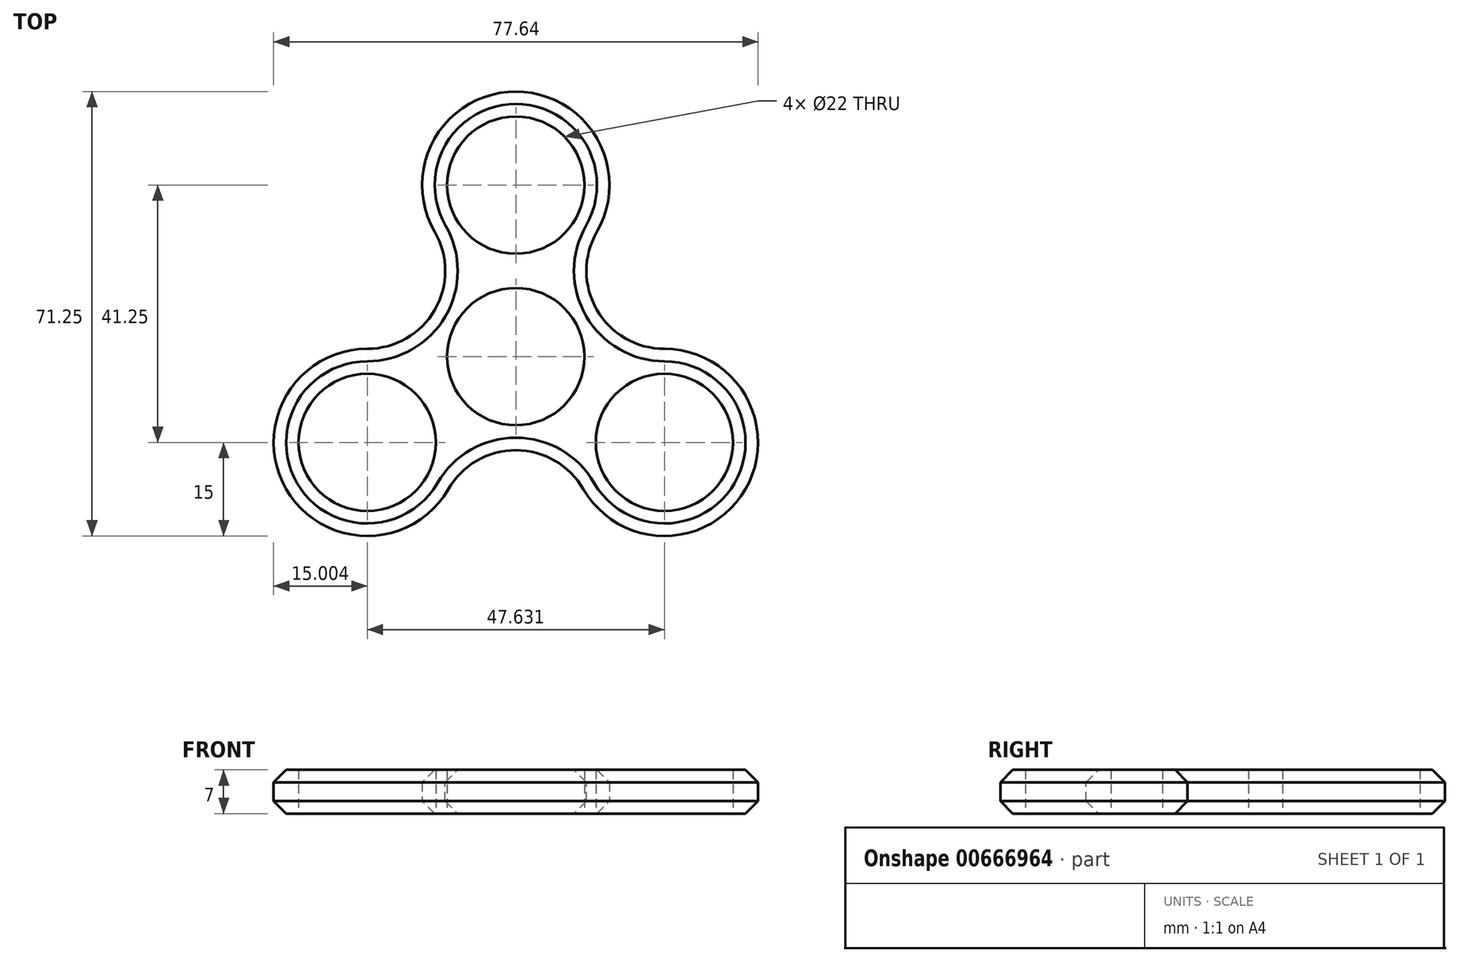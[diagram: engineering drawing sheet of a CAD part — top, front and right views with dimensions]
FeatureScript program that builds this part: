
annotation { "Feature Type Name" : "Feature", "Feature Type Description" : "" }
export const myFeature = defineFeature(function(context is Context, id is Id, definition is map)
    precondition{}
    {
        {
            var Q0;
            Q0=qCreatedBy(makeId("Top.planeOp"),FACE);
            var sketch = newSketch(context, id + "F0", { "sketchPlane" : qUnion([Q0])});
            skCircle(sketch, "E0", {"center": v(0, 0) * mm, "radius": 11 * mm});
            skLineSegment(sketch, "E1", {"start": v(0, 0) * mm, "end": v(0, 27.5) * mm, "construction": true});
            skCircle(sketch, "E2", {"center": v(0, 27.5) * mm, "radius": 11 * mm});
            skCircle(sketch, "E3.1.0", {"center": v(-23.82, -13.75) * mm, "radius": 11 * mm});
            skCircle(sketch, "E3.2.0", {"center": v(23.82, -13.75) * mm, "radius": 11 * mm});
            skCircle(sketch, "E4", {"center": v(0, 0) * mm, "radius": 15 * mm});
            skCircle(sketch, "E5", {"center": v(0, 27.5) * mm, "radius": 15 * mm});
            skCircle(sketch, "E6.1.0", {"center": v(-23.82, -13.75) * mm, "radius": 15 * mm});
            skCircle(sketch, "E6.2.0", {"center": v(23.82, -13.75) * mm, "radius": 15 * mm});
            skSolve(sketch);
        }
        {
            var Q0;
            Q0=qSketchRegion(id+"F0",true);
            extrude(context, id + "F1", {"entities" : qUnion([Q0]), "depth" : 7 * mm, "offsetDistance" : 25 * mm});
        }
        {
            var Q0;
            {var subQ0=sQuery(id+"F0.wireOp",EDGE,"E5");var subQ1=sQuery(id+"F0.wireOp",EDGE,"E4");Q0=makeQuery(id+"F1.opExtrude","SWEPT_EDGE",EDGE,{"disambiguationData":[OSD([subQ1,subQ0]),TDD([makeQuery(id+"F0.imprint","INTERSECT",VERTEX,{"disambiguationData":[OD(1.0)],"derivedFrom":[subQ1,subQ0]})])]});}
            var Q1;
            {var subQ0=sQuery(id+"F0.wireOp",EDGE,"E6.2.0");var subQ1=sQuery(id+"F0.wireOp",EDGE,"E4");Q1=makeQuery(id+"F1.opExtrude","SWEPT_EDGE",EDGE,{"disambiguationData":[OSD([subQ1,subQ0]),TDD([makeQuery(id+"F0.imprint","INTERSECT",VERTEX,{"disambiguationData":[OD(1.0)],"derivedFrom":[subQ1,subQ0]})])]});}
            var Q2;
            {var subQ0=sQuery(id+"F0.wireOp",EDGE,"E6.1.0");var subQ1=sQuery(id+"F0.wireOp",EDGE,"E4");Q2=makeQuery(id+"F1.opExtrude","SWEPT_EDGE",EDGE,{"disambiguationData":[OSD([subQ1,subQ0]),TDD([makeQuery(id+"F0.imprint","INTERSECT",VERTEX,{"disambiguationData":[OD(0.0)],"derivedFrom":[subQ1,subQ0]})])]});}
            var Q3;
            {var subQ0=sQuery(id+"F0.wireOp",EDGE,"E5");var subQ1=sQuery(id+"F0.wireOp",EDGE,"E4");Q3=makeQuery(id+"F1.opExtrude","SWEPT_EDGE",EDGE,{"disambiguationData":[OSD([subQ1,subQ0]),TDD([makeQuery(id+"F0.imprint","INTERSECT",VERTEX,{"disambiguationData":[OD(0.0)],"derivedFrom":[subQ1,subQ0]})])]});}
            var Q4;
            {var subQ0=sQuery(id+"F0.wireOp",EDGE,"E6.1.0");var subQ1=sQuery(id+"F0.wireOp",EDGE,"E4");Q4=makeQuery(id+"F1.opExtrude","SWEPT_EDGE",EDGE,{"disambiguationData":[OSD([subQ1,subQ0]),TDD([makeQuery(id+"F0.imprint","INTERSECT",VERTEX,{"disambiguationData":[OD(1.0)],"derivedFrom":[subQ1,subQ0]})])]});}
            var Q5;
            {var subQ0=sQuery(id+"F0.wireOp",EDGE,"E6.2.0");var subQ1=sQuery(id+"F0.wireOp",EDGE,"E4");Q5=makeQuery(id+"F1.opExtrude","SWEPT_EDGE",EDGE,{"disambiguationData":[OSD([subQ1,subQ0]),TDD([makeQuery(id+"F0.imprint","INTERSECT",VERTEX,{"disambiguationData":[OD(0.0)],"derivedFrom":[subQ1,subQ0]})])]});}
            fillet(context, id + "F2", {"entities" : qUnion([Q0, Q1, Q2, Q3, Q4, Q5]), "radius" : 12.5 * mm, "tangentPropagation" : true, "allowEdgeOverflow" : false});
        }
        {
            var Q0;
            {var subQ0=sQuery(id+"F0.wireOp",EDGE,"E6.1.0");var subQ1=sQuery(id+"F0.wireOp",EDGE,"E4");Q0=makeQuery(id+"F2.opFillet","BLEND_EDGE",EDGE,{"blendedFrom":[makeQuery(id+"F1.opExtrude","SWEPT_EDGE",EDGE,{"disambiguationData":[OSD([subQ1,subQ0]),TDD([makeQuery(id+"F0.imprint","INTERSECT",VERTEX,{"disambiguationData":[OD(1.0)],"derivedFrom":[subQ1,subQ0]})])]}),makeQuery(id+"F1.opExtrude","CAP_FACE",FACE,{"disambiguationData":[OSD([sQuery(id+"F0.wireOp",EDGE,"E0"),sQuery(id+"F0.wireOp",EDGE,"E2"),sQuery(id+"F0.wireOp",EDGE,"E3.1.0"),sQuery(id+"F0.wireOp",EDGE,"E3.2.0"),subQ1,sQuery(id+"F0.wireOp",EDGE,"E5"),subQ0,sQuery(id+"F0.wireOp",EDGE,"E6.2.0")])],"isStart":true})],"blendedInto":[makeQuery(id+"F1.opExtrude","CAP_FACE",FACE,{"disambiguationData":[OSD([sQuery(id+"F0.wireOp",EDGE,"E0"),sQuery(id+"F0.wireOp",EDGE,"E2"),sQuery(id+"F0.wireOp",EDGE,"E3.1.0"),sQuery(id+"F0.wireOp",EDGE,"E3.2.0"),subQ1,sQuery(id+"F0.wireOp",EDGE,"E5"),subQ0,sQuery(id+"F0.wireOp",EDGE,"E6.2.0")])],"isStart":true})]});}
            var Q1;
            {var subQ0=sQuery(id+"F0.wireOp",EDGE,"E6.1.0");var subQ1=sQuery(id+"F0.wireOp",EDGE,"E4");Q1=makeQuery(id+"F2.opFillet","BLEND_EDGE",EDGE,{"blendedFrom":[makeQuery(id+"F1.opExtrude","SWEPT_EDGE",EDGE,{"disambiguationData":[OSD([subQ1,subQ0]),TDD([makeQuery(id+"F0.imprint","INTERSECT",VERTEX,{"disambiguationData":[OD(1.0)],"derivedFrom":[subQ1,subQ0]})])]}),makeQuery(id+"F1.opExtrude","CAP_FACE",FACE,{"disambiguationData":[OSD([sQuery(id+"F0.wireOp",EDGE,"E0"),sQuery(id+"F0.wireOp",EDGE,"E2"),sQuery(id+"F0.wireOp",EDGE,"E3.1.0"),sQuery(id+"F0.wireOp",EDGE,"E3.2.0"),subQ1,sQuery(id+"F0.wireOp",EDGE,"E5"),subQ0,sQuery(id+"F0.wireOp",EDGE,"E6.2.0")])],"isStart":false})],"blendedInto":[makeQuery(id+"F1.opExtrude","CAP_FACE",FACE,{"disambiguationData":[OSD([sQuery(id+"F0.wireOp",EDGE,"E0"),sQuery(id+"F0.wireOp",EDGE,"E2"),sQuery(id+"F0.wireOp",EDGE,"E3.1.0"),sQuery(id+"F0.wireOp",EDGE,"E3.2.0"),subQ1,sQuery(id+"F0.wireOp",EDGE,"E5"),subQ0,sQuery(id+"F0.wireOp",EDGE,"E6.2.0")])],"isStart":false})]});}
            chamfer(context, id + "F3", {"entities" : qUnion([Q0, Q1]), "width" : 2 * mm, "tangentPropagation" : true});
        }
    });
